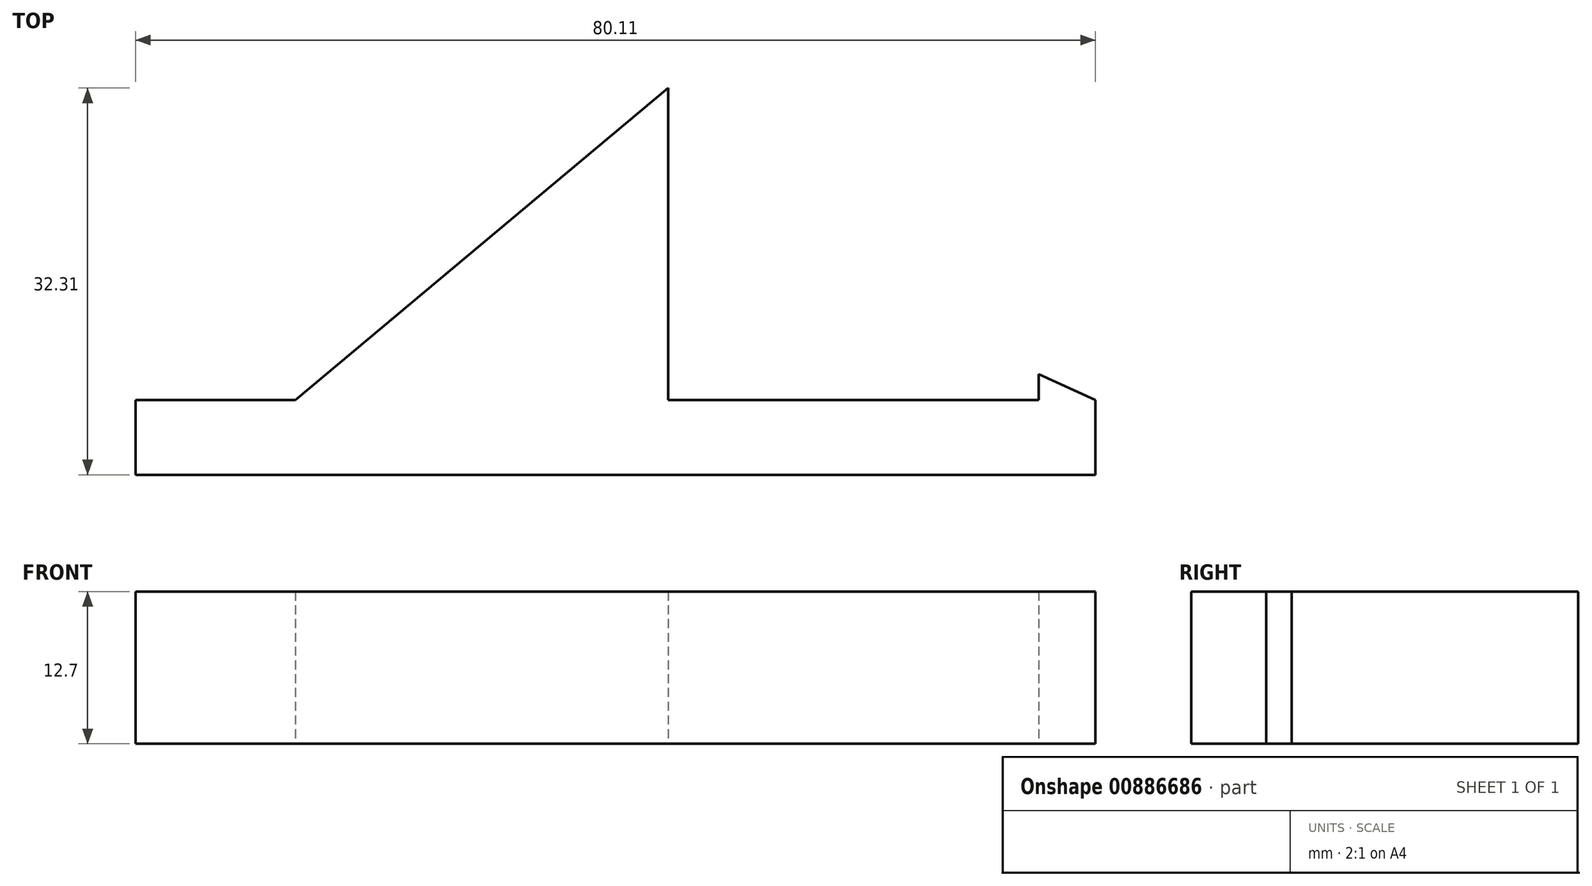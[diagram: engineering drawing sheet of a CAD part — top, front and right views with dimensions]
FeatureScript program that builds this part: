
annotation { "Feature Type Name" : "Feature", "Feature Type Description" : "" }
export const myFeature = defineFeature(function(context is Context, id is Id, definition is map)
    precondition{}
    {
        {
            var Q0;
            Q0=qCreatedBy(makeId("Top.planeOp"),FACE);
            var sketch = newSketch(context, id + "F0", { "sketchPlane" : qUnion([Q0])});
            skLineSegment(sketch, "E0", {"start": v(-44.47, 6.25) * mm, "end": v(35.64, 6.25) * mm});
            skLineSegment(sketch, "E1", {"start": v(-44.47, 6.25) * mm, "end": v(-44.47, 0) * mm});
            skLineSegment(sketch, "E2", {"start": v(-44.47, 0) * mm, "end": v(35.64, 0) * mm});
            skLineSegment(sketch, "E3", {"start": v(35.64, 6.25) * mm, "end": v(35.64, 0) * mm});
            skLineSegment(sketch, "E4", {"start": v(0, 6.25) * mm, "end": v(0, 32.3) * mm});
            skLineSegment(sketch, "E5", {"start": v(0, 32.3) * mm, "end": v(-31.12, 6.25) * mm});
            skLineSegment(sketch, "E6", {"start": v(30.9, 6.25) * mm, "end": v(30.9, 8.4) * mm});
            skLineSegment(sketch, "E7", {"start": v(30.9, 8.4) * mm, "end": v(35.64, 6.25) * mm});
            skSolve(sketch);
        }
        {
            var Q0;
            Q0 = qSketchRegion(id + "F0", true);
            extrude(context, id + "F1", {"entities" : qUnion([Q0]), "depth" : 12.7 * mm, "offsetDistance" : 25.4 * mm});
        }
    });
